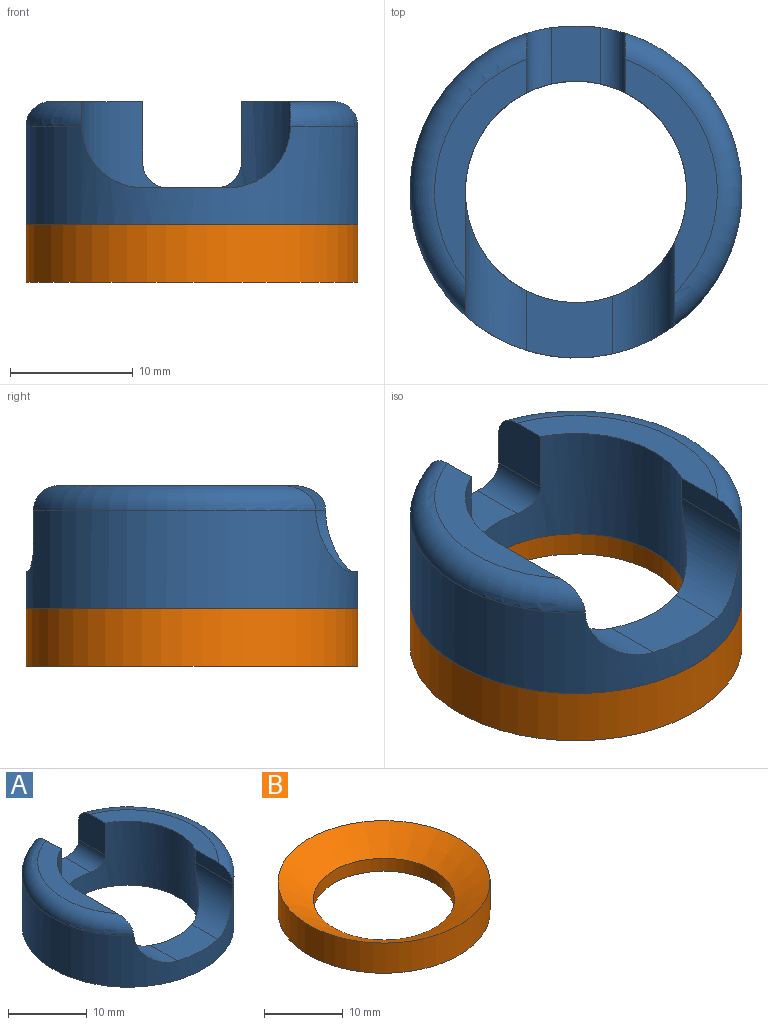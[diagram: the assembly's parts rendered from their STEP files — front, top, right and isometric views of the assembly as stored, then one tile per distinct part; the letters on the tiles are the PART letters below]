
ASSEMBLY  parts=2 mates=1
PART A: 17 faces, bbox 29.2x27.5x10 mm
  f0: plane 17.94x7.5mm, normal (0,0,1), area 42.2mm2, adj f4,f6,f8,f14
  f1: torus R=11.5mm, axis (0,0,1), area 86.1mm2, adj f2,f3,f7,f13
  f2: cylinder r=13.5mm len=27mm, axis (0,0,-1), area 560.6mm2, adj f1,f5,f6,f9,f10,f11,f12,f13
  f3: plane 19.04x7.5mm, normal (0,0,1), area 47.1mm2, adj f1,f4,f7,f13
  f4: cylinder r=9mm len=18mm, axis (0,0,-1), area 369.1mm2, adj f0,f3,f5,f7,f8,f9,f10,f11
  f5: plane 27x27mm, normal (0,0,-1), area 318.1mm2, adj f2,f4
  f6: torus R=11.5mm, axis (0,0,1), area 81.9mm2, adj f0,f2,f8,f14
  f7: plane 6.75x2mm, normal (-1,0,0), area 12.4mm2, adj f1,f3,f4,f10
  f8: plane 10.06x2mm, normal (1,0,0), area 18.9mm2, adj f0,f4,f6,f11
  f9: plane 7x5.44mm, normal (0,0,1), area 32.1mm2, adj f2,f4,f10,f11
  f10: cylinder r=5mm len=9.04mm, axis (0,1,0), area 44.7mm2, adj f2,f4,f7,f9
  f11: cylinder r=5mm len=12.89mm, axis (0,-1,0), area 52.4mm2, adj f2,f4,f8,f9
  f12: plane 4.73x4mm, normal (0,0,1), area 18.1mm2, adj f2,f4,f15,f16
  f13: plane 5x4.83mm, normal (-1,0,0), area 23.3mm2, adj f1,f2,f3,f4,f15
  f14: plane 5x4.83mm, normal (1,0,0), area 23.3mm2, adj f0,f2,f4,f6,f16
  f15: cylinder r=2mm len=5.29mm, axis (0,1,0), area 14.8mm2, adj f2,f4,f12,f13
  f16: cylinder r=2mm len=5.29mm, axis (0,-1,0), area 14.8mm2, adj f2,f4,f12,f14
PART B: 4 faces, bbox 27x27x4.7 mm
  f0: cylinder r=9mm len=18mm, axis (0,0,-1), area 113.1mm2, adj f2,f3
  f1: cylinder r=13.5mm len=27mm, axis (0,0,-1), area 398.7mm2, adj f2,f3
  f2: plane 27x27mm, normal (0,0,-1), area 318.1mm2, adj f0,f1
  f3: cone r=9mm half-angle=59deg, axis (0,0,1), area 370.9mm2, adj f0,f1
PLACE A t=(-1.58,0.74,-2.52)mm
PLACE B rot(axis=(1,0,0),180deg) t=(-1.58,0.74,-2.52)mm
MATE fastened B.f1 <-> A.f1  axis (0,0,1) through (-1.58,0.74,-2.52)mm
